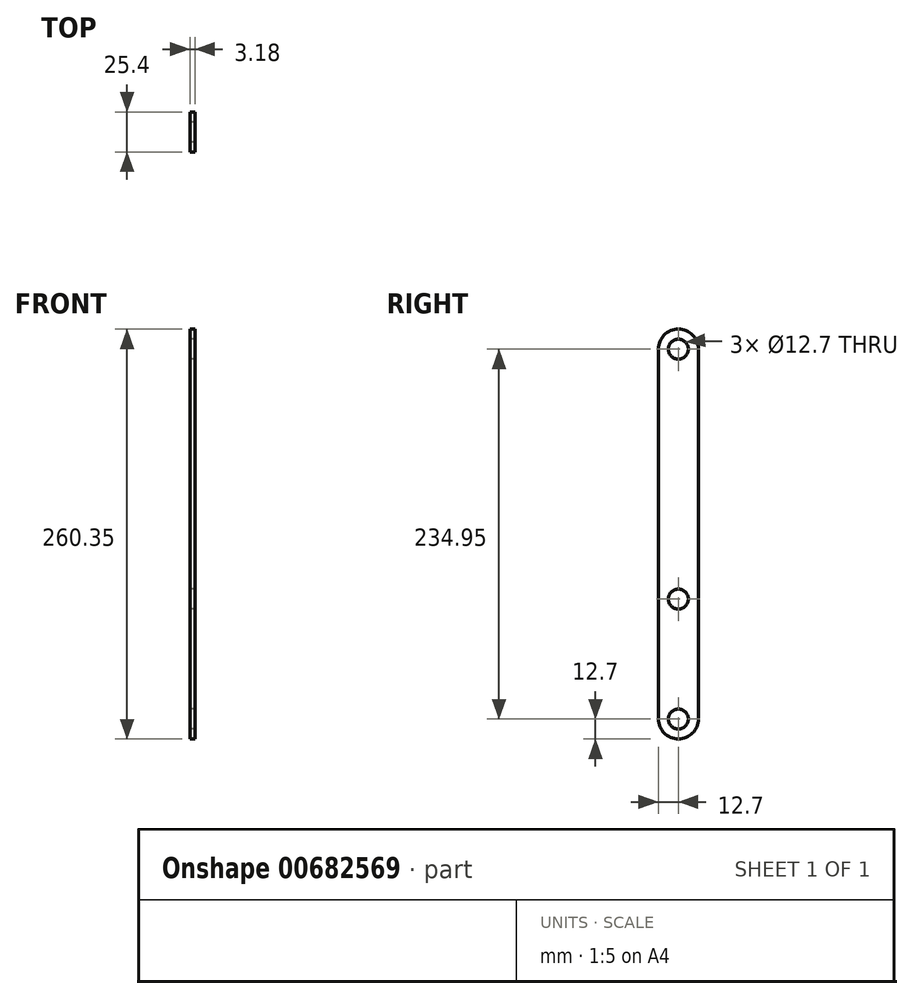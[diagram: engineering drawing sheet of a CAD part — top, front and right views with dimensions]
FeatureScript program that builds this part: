
annotation { "Feature Type Name" : "Feature", "Feature Type Description" : "" }
export const myFeature = defineFeature(function(context is Context, id is Id, definition is map)
    precondition{}
    {
        {
            var Q0;
            Q0=qCreatedBy(makeId("Right.planeOp"),FACE);
            var sketch = newSketch(context, id + "F0", { "sketchPlane" : qUnion([Q0])});
            skLineSegment(sketch, "E0.left", {"start": v(0, 0) * mm, "end": v(0, 152.4) * mm});
            skLineSegment(sketch, "E0.right", {"start": v(25.4, 6) * mm, "end": v(25.4, 152.4) * mm});
            skArc(sketch, "E1", {"start": v(25.4, 152.4) * mm, "mid": v(12.7, 165.1) * mm, "end": v(0, 152.4) * mm});
            skCircle(sketch, "E2", {"center": v(12.7, 152.4) * mm, "radius": 6.35 * mm});
            skCircle(sketch, "E3", {"center": v(12.7, -6.35) * mm, "radius": 6.35 * mm});
            skLineSegment(sketch, "E4.top", {"start": v(0, -82.55) * mm, "end": v(25.4, -82.55) * mm});
            skLineSegment(sketch, "E4.left", {"start": v(0, 0) * mm, "end": v(0, -82.55) * mm});
            skLineSegment(sketch, "E4.right", {"start": v(25.4, -9.53) * mm, "end": v(25.4, -82.55) * mm});
            skArc(sketch, "E5", {"start": v(0, -82.55) * mm, "mid": v(12.7, -95.25) * mm, "end": v(25.4, -82.55) * mm});
            skCircle(sketch, "E6", {"center": v(12.7, -82.55) * mm, "radius": 6.35 * mm});
            skLineSegment(sketch, "E7", {"start": v(25.4, 6) * mm, "end": v(25.4, -9.53) * mm});
            skSolve(sketch);
        }
        {
            var Q0;
            Q0 = qSketchRegion(id + "F0", true);
            extrude(context, id + "F1", {"entities" : qUnion([Q0]), "depth" : 3.17 * mm, "offsetDistance" : 25.4 * mm});
        }
    });
